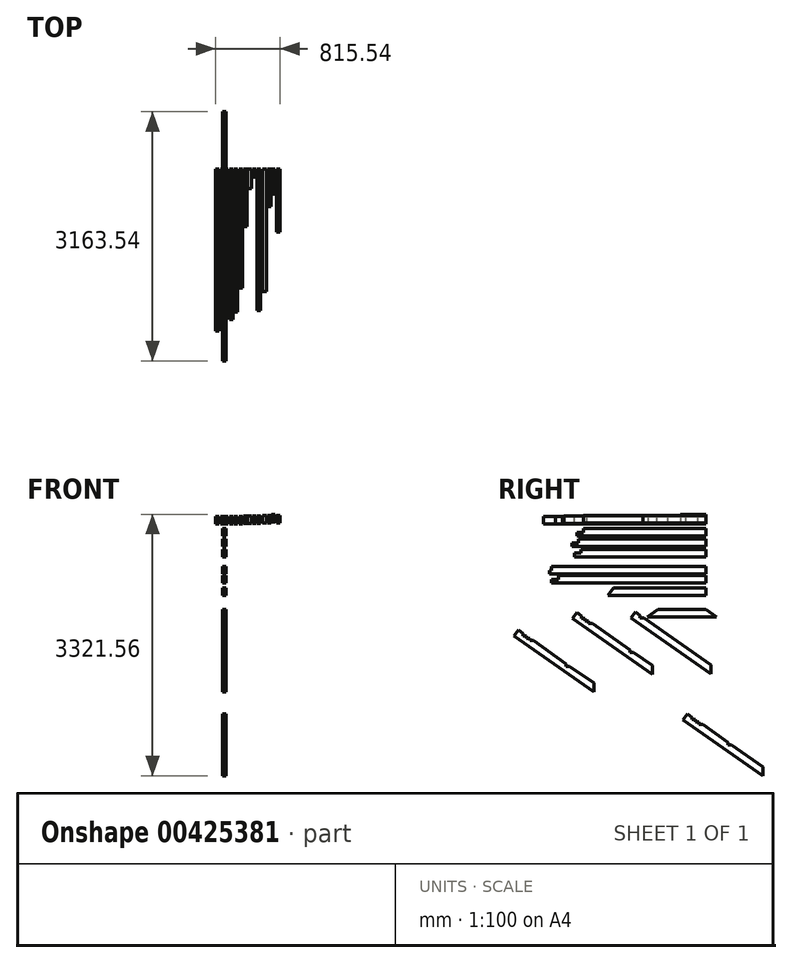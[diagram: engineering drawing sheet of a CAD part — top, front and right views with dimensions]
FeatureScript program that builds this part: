
annotation { "Feature Type Name" : "Feature", "Feature Type Description" : "" }
export const myFeature = defineFeature(function(context is Context, id is Id, definition is map)
    precondition{}
    {
        {
            var Q0;
            Q0=qCreatedBy(makeId("Front.planeOp"),FACE);
            var sketch = newSketch(context, id + "F0", { "sketchPlane" : qUnion([Q0])});
            skLineSegment(sketch, "E0.bottom", {"start": v(-87.67, 108.23) * mm, "end": v(-42.67, 108.23) * mm});
            skLineSegment(sketch, "E0.top", {"start": v(-87.67, 13.23) * mm, "end": v(-42.67, 13.23) * mm});
            skLineSegment(sketch, "E0.left", {"start": v(-87.67, 108.23) * mm, "end": v(-87.67, 13.23) * mm});
            skLineSegment(sketch, "E0.right", {"start": v(-42.67, 108.23) * mm, "end": v(-42.67, 13.23) * mm});
            skSolve(sketch);
        }
        {
            var Q0;
            Q0 = qSketchRegion(id + "F0", true);
            extrude(context, id + "F1", {"entities" : qUnion([Q0]), "depth" : 2060 * mm});
        }
        {
            var Q0;
            Q0=qCreatedBy(makeId("Front.planeOp"),FACE);
            var sketch = newSketch(context, id + "F2", { "sketchPlane" : qUnion([Q0])});
            skLineSegment(sketch, "E1.bottom", {"start": v(19.85, 13.7) * mm, "end": v(-25.15, 13.7) * mm});
            skLineSegment(sketch, "E1.top", {"start": v(19.85, 108.7) * mm, "end": v(-25.15, 108.7) * mm});
            skLineSegment(sketch, "E1.left", {"start": v(19.85, 13.7) * mm, "end": v(19.85, 108.7) * mm});
            skLineSegment(sketch, "E1.right", {"start": v(-25.15, 13.7) * mm, "end": v(-25.15, 108.7) * mm});
            skLineSegment(sketch, "E2.bottom", {"start": v(21.76, 30.66) * mm, "end": v(25.73, 30.66) * mm});
            skLineSegment(sketch, "E2.top", {"start": v(21.76, 31.99) * mm, "end": v(25.73, 31.99) * mm});
            skLineSegment(sketch, "E2.left", {"start": v(21.76, 30.66) * mm, "end": v(21.76, 31.99) * mm});
            skLineSegment(sketch, "E2.right", {"start": v(25.73, 30.66) * mm, "end": v(25.73, 31.99) * mm});
            skSolve(sketch);
        }
        {
            var Q0;
            Q0=makeQuery(id+"F2.imprint","IMPRINT",FACE,{"disambiguationData":[TD([[makeQuery(id+"F2.imprint","IMPRINT",EDGE,{"derivedFrom":sQuery(id+"F2.wireOp",EDGE,"E1.bottom")}),-1.0]])]});
            extrude(context, id + "F3", {"entities" : qUnion([Q0]), "depth" : 1670 * mm});
        }
        {
            var Q0;
            Q0=qCreatedBy(makeId("Front.planeOp"),FACE);
            var sketch = newSketch(context, id + "F4", { "sketchPlane" : qUnion([Q0])});
            skLineSegment(sketch, "E3.bottom", {"start": v(28.2, 109.72) * mm, "end": v(73.2, 109.72) * mm});
            skLineSegment(sketch, "E3.top", {"start": v(28.2, 14.72) * mm, "end": v(73.2, 14.72) * mm});
            skLineSegment(sketch, "E3.left", {"start": v(28.2, 109.72) * mm, "end": v(28.2, 14.72) * mm});
            skLineSegment(sketch, "E3.right", {"start": v(73.2, 109.72) * mm, "end": v(73.2, 14.72) * mm});
            skSolve(sketch);
        }
        {
            var Q0;
            Q0=makeQuery(id+"F4.imprint","IMPRINT",FACE,{"disambiguationData":[TD([[makeQuery(id+"F4.imprint","IMPRINT",EDGE,{"derivedFrom":sQuery(id+"F4.wireOp",EDGE,"E3.bottom")}),-1.0]])]});
            extrude(context, id + "F5", {"entities" : qUnion([Q0]), "depth" : 627 * mm});
        }
        {
            var Q0;
            Q0=qCreatedBy(makeId("Front.planeOp"),FACE);
            var sketch = newSketch(context, id + "F6", { "sketchPlane" : qUnion([Q0])});
            skLineSegment(sketch, "E4.bottom", {"start": v(86.64, 15.8) * mm, "end": v(131.64, 15.8) * mm});
            skLineSegment(sketch, "E4.top", {"start": v(86.64, 110.8) * mm, "end": v(131.64, 110.8) * mm});
            skLineSegment(sketch, "E4.left", {"start": v(86.64, 15.8) * mm, "end": v(86.64, 110.8) * mm});
            skLineSegment(sketch, "E4.right", {"start": v(131.64, 15.8) * mm, "end": v(131.64, 110.8) * mm});
            skSolve(sketch);
        }
        {
            var Q0;
            Q0=makeQuery(id+"F6.imprint","IMPRINT",FACE,{"disambiguationData":[TD([[makeQuery(id+"F6.imprint","IMPRINT",EDGE,{"derivedFrom":sQuery(id+"F6.wireOp",EDGE,"E4.bottom")}),1.0]])]});
            extrude(context, id + "F7", {"entities" : qUnion([Q0]), "depth" : 1910 * mm});
        }
        {
            var Q0;
            Q0=qCreatedBy(makeId("Front.planeOp"),FACE);
            var sketch = newSketch(context, id + "F8", { "sketchPlane" : qUnion([Q0])});
            skLineSegment(sketch, "E5.bottom", {"start": v(145.45, 16.95) * mm, "end": v(190.45, 16.95) * mm});
            skLineSegment(sketch, "E5.top", {"start": v(145.45, 111.95) * mm, "end": v(190.45, 111.95) * mm});
            skLineSegment(sketch, "E5.left", {"start": v(145.45, 16.95) * mm, "end": v(145.45, 111.95) * mm});
            skLineSegment(sketch, "E5.right", {"start": v(190.45, 16.95) * mm, "end": v(190.45, 111.95) * mm});
            skSolve(sketch);
        }
        {
            var Q0;
            Q0=qCreatedBy(makeId("Front.planeOp"),FACE);
            var sketch = newSketch(context, id + "F9", { "sketchPlane" : qUnion([Q0])});
            skLineSegment(sketch, "E6.bottom", {"start": v(206.57, 16.95) * mm, "end": v(251.57, 16.95) * mm});
            skLineSegment(sketch, "E6.top", {"start": v(206.57, 111.95) * mm, "end": v(251.57, 111.95) * mm});
            skLineSegment(sketch, "E6.left", {"start": v(206.57, 16.95) * mm, "end": v(206.57, 111.95) * mm});
            skLineSegment(sketch, "E6.right", {"start": v(251.57, 16.95) * mm, "end": v(251.57, 111.95) * mm});
            skSolve(sketch);
        }
        {
            var Q0;
            Q0=makeQuery(id+"F8.imprint","IMPRINT",FACE,{"disambiguationData":[TD([[makeQuery(id+"F8.imprint","IMPRINT",EDGE,{"derivedFrom":sQuery(id+"F8.wireOp",EDGE,"E5.bottom")}),1.0]])]});
            extrude(context, id + "F10", {"entities" : qUnion([Q0]), "depth" : 1820 * mm});
        }
        {
            var Q0;
            Q0=makeQuery(id+"F9.imprint","IMPRINT",FACE,{"disambiguationData":[TD([[makeQuery(id+"F9.imprint","IMPRINT",EDGE,{"derivedFrom":sQuery(id+"F9.wireOp",EDGE,"E6.bottom")}),1.0]])]});
            extrude(context, id + "F11", {"entities" : qUnion([Q0]), "depth" : 1510 * mm});
        }
        {
            var Q0;
            Q0=qCreatedBy(makeId("Front.planeOp"),FACE);
            var sketch = newSketch(context, id + "F12", { "sketchPlane" : qUnion([Q0])});
            skLineSegment(sketch, "E7.bottom", {"start": v(263.6, 113.4) * mm, "end": v(308.6, 113.4) * mm});
            skLineSegment(sketch, "E7.top", {"start": v(263.6, 18.4) * mm, "end": v(308.6, 18.4) * mm});
            skLineSegment(sketch, "E7.left", {"start": v(263.6, 113.4) * mm, "end": v(263.6, 18.4) * mm});
            skLineSegment(sketch, "E7.right", {"start": v(308.6, 113.4) * mm, "end": v(308.6, 18.4) * mm});
            skSolve(sketch);
        }
        {
            var Q0;
            Q0=qCreatedBy(makeId("Front.planeOp"),FACE);
            var sketch = newSketch(context, id + "F13", { "sketchPlane" : qUnion([Q0])});
            skLineSegment(sketch, "E8.bottom", {"start": v(320.45, 18.8) * mm, "end": v(365.45, 18.8) * mm});
            skLineSegment(sketch, "E8.top", {"start": v(320.45, 113.8) * mm, "end": v(365.45, 113.8) * mm});
            skLineSegment(sketch, "E8.left", {"start": v(320.45, 18.8) * mm, "end": v(320.45, 113.8) * mm});
            skLineSegment(sketch, "E8.right", {"start": v(365.45, 18.8) * mm, "end": v(365.45, 113.8) * mm});
            skSolve(sketch);
        }
        {
            var Q0;
            Q0=makeQuery(id+"F12.imprint","IMPRINT",FACE,{"disambiguationData":[TD([[makeQuery(id+"F12.imprint","IMPRINT",EDGE,{"derivedFrom":sQuery(id+"F12.wireOp",EDGE,"E7.bottom")}),-1.0]])]});
            extrude(context, id + "F14", {"entities" : qUnion([Q0]), "depth" : 733 * mm});
        }
        {
            var Q0;
            Q0=makeQuery(id+"F13.imprint","IMPRINT",FACE,{"disambiguationData":[TD([[makeQuery(id+"F13.imprint","IMPRINT",EDGE,{"derivedFrom":sQuery(id+"F13.wireOp",EDGE,"E8.bottom")}),1.0]])]});
            extrude(context, id + "F15", {"entities" : qUnion([Q0]), "depth" : 250 * mm});
        }
        {
            var Q0;
            Q0=qCreatedBy(makeId("Front.planeOp"),FACE);
            var sketch = newSketch(context, id + "F16", { "sketchPlane" : qUnion([Q0])});
            skLineSegment(sketch, "E9.bottom", {"start": v(381.29, 20.1) * mm, "end": v(426.29, 20.1) * mm});
            skLineSegment(sketch, "E9.top", {"start": v(381.29, 115.1) * mm, "end": v(426.29, 115.1) * mm});
            skLineSegment(sketch, "E9.left", {"start": v(381.29, 20.1) * mm, "end": v(381.29, 115.1) * mm});
            skLineSegment(sketch, "E9.right", {"start": v(426.29, 20.1) * mm, "end": v(426.29, 115.1) * mm});
            skSolve(sketch);
        }
        {
            var Q0;
            Q0=makeQuery(id+"F16.imprint","IMPRINT",FACE,{"disambiguationData":[TD([[makeQuery(id+"F16.imprint","IMPRINT",EDGE,{"derivedFrom":sQuery(id+"F16.wireOp",EDGE,"E9.bottom")}),1.0]])]});
            extrude(context, id + "F17", {"entities" : qUnion([Q0]), "depth" : 100 * mm});
        }
        {
            var Q0;
            Q0=qCreatedBy(makeId("Front.planeOp"),FACE);
            var sketch = newSketch(context, id + "F18", { "sketchPlane" : qUnion([Q0])});
            skLineSegment(sketch, "E10.bottom", {"start": v(440.57, 23.4) * mm, "end": v(485.57, 23.4) * mm});
            skLineSegment(sketch, "E10.top", {"start": v(440.57, 118.4) * mm, "end": v(485.57, 118.4) * mm});
            skLineSegment(sketch, "E10.left", {"start": v(440.57, 23.4) * mm, "end": v(440.57, 118.4) * mm});
            skLineSegment(sketch, "E10.right", {"start": v(485.57, 23.4) * mm, "end": v(485.57, 118.4) * mm});
            skSolve(sketch);
        }
        {
            var Q0;
            Q0=qCreatedBy(makeId("Front.planeOp"),FACE);
            var sketch = newSketch(context, id + "F19", { "sketchPlane" : qUnion([Q0])});
            skLineSegment(sketch, "E11.bottom", {"start": v(510.5, 25.25) * mm, "end": v(555.5, 25.25) * mm});
            skLineSegment(sketch, "E11.top", {"start": v(510.5, 120.25) * mm, "end": v(555.5, 120.25) * mm});
            skLineSegment(sketch, "E11.left", {"start": v(510.5, 25.25) * mm, "end": v(510.5, 120.25) * mm});
            skLineSegment(sketch, "E11.right", {"start": v(555.5, 25.25) * mm, "end": v(555.5, 120.25) * mm});
            skSolve(sketch);
        }
        {
            var Q0;
            Q0=makeQuery(id+"F18.imprint","IMPRINT",FACE,{"disambiguationData":[TD([[makeQuery(id+"F18.imprint","IMPRINT",EDGE,{"derivedFrom":sQuery(id+"F18.wireOp",EDGE,"E10.bottom")}),1.0]])]});
            extrude(context, id + "F20", {"entities" : qUnion([Q0]), "depth" : 1800 * mm});
        }
        {
            var Q0;
            Q0=makeQuery(id+"F19.imprint","IMPRINT",FACE,{"disambiguationData":[TD([[makeQuery(id+"F19.imprint","IMPRINT",EDGE,{"derivedFrom":sQuery(id+"F19.wireOp",EDGE,"E11.bottom")}),1.0]])]});
            extrude(context, id + "F21", {"entities" : qUnion([Q0]), "depth" : 1554 * mm});
        }
        {
            var Q0;
            Q0=qCreatedBy(makeId("Right.planeOp"),FACE);
            var sketch = newSketch(context, id + "F22", { "sketchPlane" : qUnion([Q0])});
            skLineSegment(sketch, "E12", {"start": v(0, -136.78) * mm, "end": v(-1638, -136.78) * mm});
            skLineSegment(sketch, "E13", {"start": v(-1638, -136.78) * mm, "end": v(-1638, -91.78) * mm});
            skLineSegment(sketch, "E14", {"start": v(-1638, -91.78) * mm, "end": v(-1554, -91.78) * mm});
            skLineSegment(sketch, "E15", {"start": v(-1554, -91.78) * mm, "end": v(-1554, -46.78) * mm});
            skLineSegment(sketch, "E16", {"start": v(-1554, -46.78) * mm, "end": v(0, -46.78) * mm});
            skLineSegment(sketch, "E17", {"start": v(0, -46.78) * mm, "end": v(0, -136.78) * mm});
            skSolve(sketch);
        }
        {
            var Q0;
            Q0=makeQuery(id+"F22.imprint","IMPRINT",FACE,{"disambiguationData":[TD([[makeQuery(id+"F22.imprint","IMPRINT",EDGE,{"derivedFrom":sQuery(id+"F22.wireOp",EDGE,"E12")}),-1.0]])]});
            extrude(context, id + "F23", {"entities" : qUnion([Q0]), "depth" : 45 * mm});
        }
        {
            var Q0;
            Q0=qCreatedBy(makeId("Right.planeOp"),FACE);
            var sketch = newSketch(context, id + "F24", { "sketchPlane" : qUnion([Q0])});
            skLineSegment(sketch, "E18", {"start": v(0, -312.27) * mm, "end": v(0, -407.27) * mm});
            skLineSegment(sketch, "E19", {"start": v(0, -407.27) * mm, "end": v(-1670, -407.27) * mm});
            skLineSegment(sketch, "E20", {"start": v(-1670, -407.27) * mm, "end": v(-1670, -357.27) * mm});
            skLineSegment(sketch, "E21", {"start": v(-1670, -357.27) * mm, "end": v(-1586, -357.27) * mm});
            skLineSegment(sketch, "E22", {"start": v(-1586, -357.27) * mm, "end": v(-1586, -312.27) * mm});
            skLineSegment(sketch, "E23", {"start": v(-1586, -312.27) * mm, "end": v(0, -312.27) * mm});
            skSolve(sketch);
        }
        {
            var Q0;
            Q0=makeQuery(id+"F24.imprint","IMPRINT",FACE,{"disambiguationData":[TD([[makeQuery(id+"F24.imprint","IMPRINT",EDGE,{"derivedFrom":sQuery(id+"F24.wireOp",EDGE,"E18")}),-1.0]])]});
            extrude(context, id + "F25", {"entities" : qUnion([Q0]), "depth" : 45 * mm});
        }
        {
            var Q0;
            Q0=makeQuery(id+"F23.opExtrude","SWEPT_FACE",FACE,{"disambiguationData":[OSD([sQuery(id+"F22.wireOp",EDGE,"E16")])]});
            extrude(context, id + "F26", {"entities" : qUnion([Q0]), "operationType" : NewBodyOperationType.ADD, "depth" : 5 * mm});
        }
        {
            var Q0;
            Q0=makeQuery(id+"F25.opExtrude","SWEPT_FACE",FACE,{"disambiguationData":[OSD([sQuery(id+"F24.wireOp",EDGE,"E21")])]});
            extrude(context, id + "F27", {"entities" : qUnion([Q0]), "operationType" : NewBodyOperationType.ADD, "depth" : 5 * mm});
        }
        {
            var Q0;
            Q0=qCreatedBy(makeId("Right.planeOp"),FACE);
            var sketch = newSketch(context, id + "F28", { "sketchPlane" : qUnion([Q0])});
            skLineSegment(sketch, "E24", {"start": v(0, -179.4) * mm, "end": v(0, -274.4) * mm});
            skLineSegment(sketch, "E25", {"start": v(0, -274.4) * mm, "end": v(-1702, -274.4) * mm});
            skLineSegment(sketch, "E26", {"start": v(-1702, -274.4) * mm, "end": v(-1702, -224.4) * mm});
            skLineSegment(sketch, "E27", {"start": v(-1702, -224.4) * mm, "end": v(-1618, -224.4) * mm});
            skLineSegment(sketch, "E28", {"start": v(-1618, -224.4) * mm, "end": v(-1618, -179.4) * mm});
            skLineSegment(sketch, "E29", {"start": v(-1618, -179.4) * mm, "end": v(0, -179.4) * mm});
            skSolve(sketch);
        }
        {
            var Q0;
            Q0=makeQuery(id+"F28.imprint","IMPRINT",FACE,{"disambiguationData":[TD([[makeQuery(id+"F28.imprint","IMPRINT",EDGE,{"derivedFrom":sQuery(id+"F28.wireOp",EDGE,"E24")}),-1.0]])]});
            extrude(context, id + "F29", {"entities" : qUnion([Q0]), "depth" : 45 * mm});
        }
        {
            var Q0;
            Q0=qCreatedBy(makeId("Right.planeOp"),FACE);
            var sketch = newSketch(context, id + "F30", { "sketchPlane" : qUnion([Q0])});
            skLineSegment(sketch, "E30", {"start": v(0, -526.73) * mm, "end": v(0, -621.73) * mm});
            skLineSegment(sketch, "E31", {"start": v(0, -621.73) * mm, "end": v(-1985, -621.73) * mm});
            skLineSegment(sketch, "E32", {"start": v(-1985, -621.73) * mm, "end": v(-1985, -576.73) * mm});
            skLineSegment(sketch, "E33", {"start": v(-1985, -576.73) * mm, "end": v(-1962, -576.73) * mm});
            skLineSegment(sketch, "E34", {"start": v(-1962, -576.73) * mm, "end": v(-1962, -526.73) * mm});
            skLineSegment(sketch, "E35", {"start": v(-1962, -526.73) * mm, "end": v(0, -526.73) * mm});
            skSolve(sketch);
        }
        {
            var Q0;
            Q0=makeQuery(id+"F30.imprint","IMPRINT",FACE,{"disambiguationData":[TD([[makeQuery(id+"F30.imprint","IMPRINT",EDGE,{"derivedFrom":sQuery(id+"F30.wireOp",EDGE,"E30")}),-1.0]])]});
            extrude(context, id + "F31", {"entities" : qUnion([Q0]), "depth" : 45 * mm});
        }
        {
            var Q0;
            Q0=qCreatedBy(makeId("Front.planeOp"),FACE);
            var sketch = newSketch(context, id + "F32", { "sketchPlane" : qUnion([Q0])});
            skLineSegment(sketch, "E36.bottom", {"start": v(572.97, 27.63) * mm, "end": v(617.97, 27.63) * mm});
            skLineSegment(sketch, "E36.top", {"start": v(572.97, 122.63) * mm, "end": v(617.97, 122.63) * mm});
            skLineSegment(sketch, "E36.left", {"start": v(572.97, 27.63) * mm, "end": v(572.97, 122.63) * mm});
            skLineSegment(sketch, "E36.right", {"start": v(617.97, 27.63) * mm, "end": v(617.97, 122.63) * mm});
            skSolve(sketch);
        }
        {
            var Q0;
            Q0=makeQuery(id+"F32.imprint","IMPRINT",FACE,{"disambiguationData":[TD([[makeQuery(id+"F32.imprint","IMPRINT",EDGE,{"derivedFrom":sQuery(id+"F32.wireOp",EDGE,"E36.bottom")}),1.0]])]});
            extrude(context, id + "F33", {"entities" : qUnion([Q0]), "depth" : 480 * mm});
        }
        {
            var Q0;
            Q0=makeQuery(id+"F27.opExtrude","CAP_FACE",FACE,{"disambiguationData":[OSD([sQuery(id+"F24.wireOp",EDGE,"E21")])],"isStart":false});
            extrude(context, id + "F34", {"entities" : qUnion([Q0]), "operationType" : NewBodyOperationType.ADD, "depth" : -5 * mm});
        }
        {
            var Q0;
            Q0=makeQuery(id+"F27.opExtrude","CAP_FACE",FACE,{"disambiguationData":[OSD([sQuery(id+"F24.wireOp",EDGE,"E21")])],"isStart":false});
            extrude(context, id + "F35", {"entities" : qUnion([Q0]), "operationType" : NewBodyOperationType.ADD, "depth" : -5 * mm});
        }
        {
            var Q0;
            Q0=qCreatedBy(makeId("Right.planeOp"),FACE);
            var sketch = newSketch(context, id + "F36", { "sketchPlane" : qUnion([Q0])});
            skLineSegment(sketch, "E37", {"start": v(0, -642.9) * mm, "end": v(0, -737.9) * mm});
            skLineSegment(sketch, "E38", {"start": v(0, -737.9) * mm, "end": v(-1958, -737.9) * mm});
            skLineSegment(sketch, "E39", {"start": v(-1958, -737.9) * mm, "end": v(-1958, -692.9) * mm});
            skLineSegment(sketch, "E40", {"start": v(-1958, -692.9) * mm, "end": v(-1874, -692.9) * mm});
            skLineSegment(sketch, "E41", {"start": v(-1874, -692.9) * mm, "end": v(-1874, -642.9) * mm});
            skLineSegment(sketch, "E42", {"start": v(-1874, -642.9) * mm, "end": v(0, -642.9) * mm});
            skSolve(sketch);
        }
        {
            var Q0;
            Q0=makeQuery(id+"F36.imprint","IMPRINT",FACE,{"disambiguationData":[TD([[makeQuery(id+"F36.imprint","IMPRINT",EDGE,{"derivedFrom":sQuery(id+"F36.wireOp",EDGE,"E37")}),-1.0]])]});
            extrude(context, id + "F37", {"entities" : qUnion([Q0]), "depth" : 45 * mm});
        }
        {
            var Q0;
            Q0=qCreatedBy(makeId("Front.planeOp"),FACE);
            var sketch = newSketch(context, id + "F38", { "sketchPlane" : qUnion([Q0])});
            skLineSegment(sketch, "E43.bottom", {"start": v(623.9, 136.83) * mm, "end": v(668.9, 136.83) * mm});
            skLineSegment(sketch, "E43.top", {"start": v(623.9, 41.83) * mm, "end": v(668.9, 41.83) * mm});
            skLineSegment(sketch, "E43.left", {"start": v(623.9, 136.83) * mm, "end": v(623.9, 41.83) * mm});
            skLineSegment(sketch, "E43.right", {"start": v(668.9, 136.83) * mm, "end": v(668.9, 41.83) * mm});
            skSolve(sketch);
        }
        {
            var Q0;
            Q0=qCreatedBy(makeId("Front.planeOp"),FACE);
            var sketch = newSketch(context, id + "F39", { "sketchPlane" : qUnion([Q0])});
            skLineSegment(sketch, "E44.bottom", {"start": v(682.87, 124.63) * mm, "end": v(727.87, 124.63) * mm});
            skLineSegment(sketch, "E44.top", {"start": v(682.87, 29.63) * mm, "end": v(727.87, 29.63) * mm});
            skLineSegment(sketch, "E44.left", {"start": v(682.87, 124.63) * mm, "end": v(682.87, 29.63) * mm});
            skLineSegment(sketch, "E44.right", {"start": v(727.87, 124.63) * mm, "end": v(727.87, 29.63) * mm});
            skSolve(sketch);
        }
        {
            var Q0;
            Q0=makeQuery(id+"F38.imprint","IMPRINT",FACE,{"disambiguationData":[TD([[makeQuery(id+"F38.imprint","IMPRINT",EDGE,{"derivedFrom":sQuery(id+"F38.wireOp",EDGE,"E43.bottom")}),-1.0]])]});
            extrude(context, id + "F40", {"entities" : qUnion([Q0]), "depth" : 320 * mm});
        }
        {
            var Q0;
            Q0=makeQuery(id+"F39.imprint","IMPRINT",FACE,{"disambiguationData":[TD([[makeQuery(id+"F39.imprint","IMPRINT",EDGE,{"derivedFrom":sQuery(id+"F39.wireOp",EDGE,"E44.bottom")}),-1.0]])]});
            extrude(context, id + "F41", {"entities" : qUnion([Q0]), "depth" : 800 * mm});
        }
        {
            var Q0;
            Q0=qCreatedBy(makeId("Right.planeOp"),FACE);
            var sketch = newSketch(context, id + "F42", { "sketchPlane" : qUnion([Q0])});
            skLineSegment(sketch, "E45", {"start": v(0, -800.48) * mm, "end": v(0, -895.48) * mm});
            skLineSegment(sketch, "E46", {"start": v(0, -895.48) * mm, "end": v(-1240, -895.48) * mm});
            skLineSegment(sketch, "E47", {"start": v(-1240, -895.48) * mm, "end": v(-1173.5, -800.48) * mm});
            skLineSegment(sketch, "E48", {"start": v(-1173.5, -800.48) * mm, "end": v(0, -800.48) * mm});
            skSolve(sketch);
        }
        {
            var Q0;
            Q0=makeQuery(id+"F42.imprint","IMPRINT",FACE,{"disambiguationData":[TD([[makeQuery(id+"F42.imprint","IMPRINT",EDGE,{"derivedFrom":sQuery(id+"F42.wireOp",EDGE,"E45")}),-1.0]])]});
            extrude(context, id + "F43", {"entities" : qUnion([Q0]), "depth" : 45 * mm});
        }
        {
            var Q0;
            Q0=qCreatedBy(makeId("Right.planeOp"),FACE);
            var sketch = newSketch(context, id + "F44", { "sketchPlane" : qUnion([Q0])});
            skLineSegment(sketch, "E49", {"start": v(-1693.72, -1188.78) * mm, "end": v(-677.98, -1900.01) * mm});
            skLineSegment(sketch, "E50", {"start": v(-1693.72, -1188.78) * mm, "end": v(-1639.24, -1110.96) * mm});
            skLineSegment(sketch, "E51", {"start": v(-677.98, -1900.01) * mm, "end": v(-677.98, -1784.04) * mm});
            skLineSegment(sketch, "E52", {"start": v(-917.98, -1616) * mm, "end": v(-962.98, -1616) * mm});
            skLineSegment(sketch, "E53", {"start": v(-962.98, -1616) * mm, "end": v(-962.98, -1584.48) * mm});
            skLineSegment(sketch, "E54", {"start": v(-677.98, -1784.04) * mm, "end": v(-917.98, -1616) * mm});
            skLineSegment(sketch, "E55", {"start": v(-1442.98, -1248.38) * mm, "end": v(-1487.98, -1248.38) * mm});
            skLineSegment(sketch, "E56", {"start": v(-1487.98, -1248.38) * mm, "end": v(-1487.98, -1216.87) * mm});
            skLineSegment(sketch, "E57", {"start": v(-1487.98, -1216.87) * mm, "end": v(-1532.98, -1216.87) * mm});
            skLineSegment(sketch, "E58", {"start": v(-1532.98, -1216.87) * mm, "end": v(-1532.98, -1185.36) * mm});
            skLineSegment(sketch, "E59", {"start": v(-1532.98, -1185.36) * mm, "end": v(-1577.98, -1185.36) * mm});
            skLineSegment(sketch, "E60", {"start": v(-1577.98, -1185.36) * mm, "end": v(-1577.98, -1153.85) * mm});
            skLineSegment(sketch, "E61", {"start": v(-1639.24, -1110.96) * mm, "end": v(-1577.98, -1153.85) * mm});
            skLineSegment(sketch, "E62", {"start": v(-1442.98, -1248.38) * mm, "end": v(-962.98, -1584.48) * mm});
            skLineSegment(sketch, "E63", {"start": v(-949.3, -1181.73) * mm, "end": v(66.45, -1892.97) * mm});
            skLineSegment(sketch, "E64", {"start": v(-949.3, -1181.73) * mm, "end": v(-894.81, -1103.91) * mm});
            skLineSegment(sketch, "E65", {"start": v(66.45, -1892.97) * mm, "end": v(66.45, -1777) * mm});
            skLineSegment(sketch, "E66", {"start": v(66.45, -1777) * mm, "end": v(-173.55, -1608.95) * mm});
            skLineSegment(sketch, "E67", {"start": v(-788.55, -1178.32) * mm, "end": v(-833.55, -1178.32) * mm});
            skLineSegment(sketch, "E68", {"start": v(-833.55, -1178.32) * mm, "end": v(-833.55, -1146.8) * mm});
            skLineSegment(sketch, "E69", {"start": v(-894.81, -1103.91) * mm, "end": v(-833.55, -1146.8) * mm});
            skLineSegment(sketch, "E70", {"start": v(-218.55, -1577.44) * mm, "end": v(-788.55, -1178.32) * mm});
            skLineSegment(sketch, "E71", {"start": v(-218.55, -1577.44) * mm, "end": v(-173.55, -1608.95) * mm});
            skLineSegment(sketch, "E72", {"start": v(-2436.78, -1408.66) * mm, "end": v(-1421.03, -2119.9) * mm});
            skLineSegment(sketch, "E73", {"start": v(-2436.78, -1408.66) * mm, "end": v(-2382.29, -1330.84) * mm});
            skLineSegment(sketch, "E74", {"start": v(-1421.03, -2119.9) * mm, "end": v(-1421.03, -2003.92) * mm});
            skLineSegment(sketch, "E75", {"start": v(-2186.03, -1468.26) * mm, "end": v(-2231.03, -1468.26) * mm});
            skLineSegment(sketch, "E76", {"start": v(-2231.03, -1468.26) * mm, "end": v(-2231.03, -1436.75) * mm});
            skLineSegment(sketch, "E77", {"start": v(-2231.03, -1436.75) * mm, "end": v(-2276.03, -1436.75) * mm});
            skLineSegment(sketch, "E78", {"start": v(-2276.03, -1436.75) * mm, "end": v(-2276.03, -1405.24) * mm});
            skLineSegment(sketch, "E79", {"start": v(-2276.03, -1405.24) * mm, "end": v(-2321.03, -1405.24) * mm});
            skLineSegment(sketch, "E80", {"start": v(-2321.03, -1405.24) * mm, "end": v(-2321.03, -1373.73) * mm});
            skLineSegment(sketch, "E81", {"start": v(-2382.29, -1330.84) * mm, "end": v(-2321.03, -1373.73) * mm});
            skLineSegment(sketch, "E82", {"start": v(-1776.03, -1795.39) * mm, "end": v(-1731.03, -1795.39) * mm});
            skLineSegment(sketch, "E83", {"start": v(-1776.03, -1795.39) * mm, "end": v(-1776.03, -1763.03) * mm});
            skLineSegment(sketch, "E84", {"start": v(-1421.03, -2003.92) * mm, "end": v(-1731.03, -1795.39) * mm});
            skLineSegment(sketch, "E85", {"start": v(-1776.03, -1763.03) * mm, "end": v(-2186.03, -1468.26) * mm});
            skSolve(sketch);
        }
        {
            var Q0;
            Q0=qCreatedBy(makeId("Right.planeOp"),FACE);
            var sketch = newSketch(context, id + "F45", { "sketchPlane" : qUnion([Q0])});
            skLineSegment(sketch, "E86", {"start": v(-607, -1074.22) * mm, "end": v(0, -1074.22) * mm});
            skLineSegment(sketch, "E87", {"start": v(-607, -1169.22) * mm, "end": v(-742.67, -1169.22) * mm});
            skLineSegment(sketch, "E88", {"start": v(-607, -1074.22) * mm, "end": v(-742.67, -1169.22) * mm});
            skLineSegment(sketch, "E89", {"start": v(-607, -1169.22) * mm, "end": v(135.67, -1169.22) * mm});
            skLineSegment(sketch, "E90", {"start": v(0, -1074.22) * mm, "end": v(135.67, -1169.22) * mm});
            skSolve(sketch);
        }
        {
            var Q0;
            Q0=makeQuery(id+"F45.imprint","IMPRINT",FACE,{"disambiguationData":[TD([[makeQuery(id+"F45.imprint","IMPRINT",EDGE,{"derivedFrom":sQuery(id+"F45.wireOp",EDGE,"E86")}),-1.0]])]});
            extrude(context, id + "F46", {"entities" : qUnion([Q0]), "depth" : 45 * mm});
        }
        {
            var Q0;
            Q0=makeQuery(id+"F44.imprint","IMPRINT",FACE,{"disambiguationData":[TD([[makeQuery(id+"F44.imprint","IMPRINT",EDGE,{"derivedFrom":sQuery(id+"F44.wireOp",EDGE,"E63")}),1.0]])]});
            var Q1;
            Q1=makeQuery(id+"F44.imprint","IMPRINT",FACE,{"disambiguationData":[TD([[makeQuery(id+"F44.imprint","IMPRINT",EDGE,{"derivedFrom":sQuery(id+"F44.wireOp",EDGE,"E49")}),1.0]])]});
            var Q2;
            Q2=makeQuery(id+"F44.imprint","IMPRINT",FACE,{"disambiguationData":[TD([[makeQuery(id+"F44.imprint","IMPRINT",EDGE,{"derivedFrom":sQuery(id+"F44.wireOp",EDGE,"E72")}),1.0]])]});
            extrude(context, id + "F47", {"entities" : qUnion([Q0, Q1, Q2]), "depth" : 45 * mm});
        }
        {
            var Q0;
            Q0=qCreatedBy(makeId("Right.planeOp"),FACE);
            var sketch = newSketch(context, id + "F48", { "sketchPlane" : qUnion([Q0])});
            skLineSegment(sketch, "E91", {"start": v(726.76, -3184.73) * mm, "end": v(-290.14, -2475.14) * mm});
            skLineSegment(sketch, "E92", {"start": v(-290.14, -2475.14) * mm, "end": v(-235.78, -2397.23) * mm});
            skLineSegment(sketch, "E93", {"start": v(726.76, -3184.73) * mm, "end": v(726.7, -3068.84) * mm});
            skLineSegment(sketch, "E94", {"start": v(281.7, -2789.72) * mm, "end": v(326.7, -2789.72) * mm});
            skLineSegment(sketch, "E95", {"start": v(281.7, -2789.72) * mm, "end": v(281.7, -2758.32) * mm});
            skLineSegment(sketch, "E96", {"start": v(-39.26, -2534.36) * mm, "end": v(-84.26, -2534.36) * mm});
            skLineSegment(sketch, "E97", {"start": v(-84.26, -2534.36) * mm, "end": v(-84.26, -2502.96) * mm});
            skLineSegment(sketch, "E98", {"start": v(-84.26, -2502.96) * mm, "end": v(-129.26, -2502.96) * mm});
            skLineSegment(sketch, "E99", {"start": v(-129.26, -2502.96) * mm, "end": v(-129.26, -2471.56) * mm});
            skLineSegment(sketch, "E100", {"start": v(-129.26, -2471.56) * mm, "end": v(-174.26, -2471.56) * mm});
            skLineSegment(sketch, "E101", {"start": v(-174.26, -2471.56) * mm, "end": v(-174.26, -2440.16) * mm});
            skLineSegment(sketch, "E102", {"start": v(-235.78, -2397.23) * mm, "end": v(-174.26, -2440.16) * mm});
            skLineSegment(sketch, "E103", {"start": v(-39.26, -2534.36) * mm, "end": v(281.7, -2758.32) * mm});
            skLineSegment(sketch, "E104", {"start": v(326.7, -2789.72) * mm, "end": v(726.7, -3068.84) * mm});
            skSolve(sketch);
        }
        {
            var Q0;
            Q0=makeQuery(id+"F48.imprint","IMPRINT",FACE,{"disambiguationData":[TD([[makeQuery(id+"F48.imprint","IMPRINT",EDGE,{"derivedFrom":sQuery(id+"F48.wireOp",EDGE,"E91")}),-1.0]])]});
            extrude(context, id + "F49", {"entities" : qUnion([Q0]), "depth" : 45 * mm});
        }
    });
